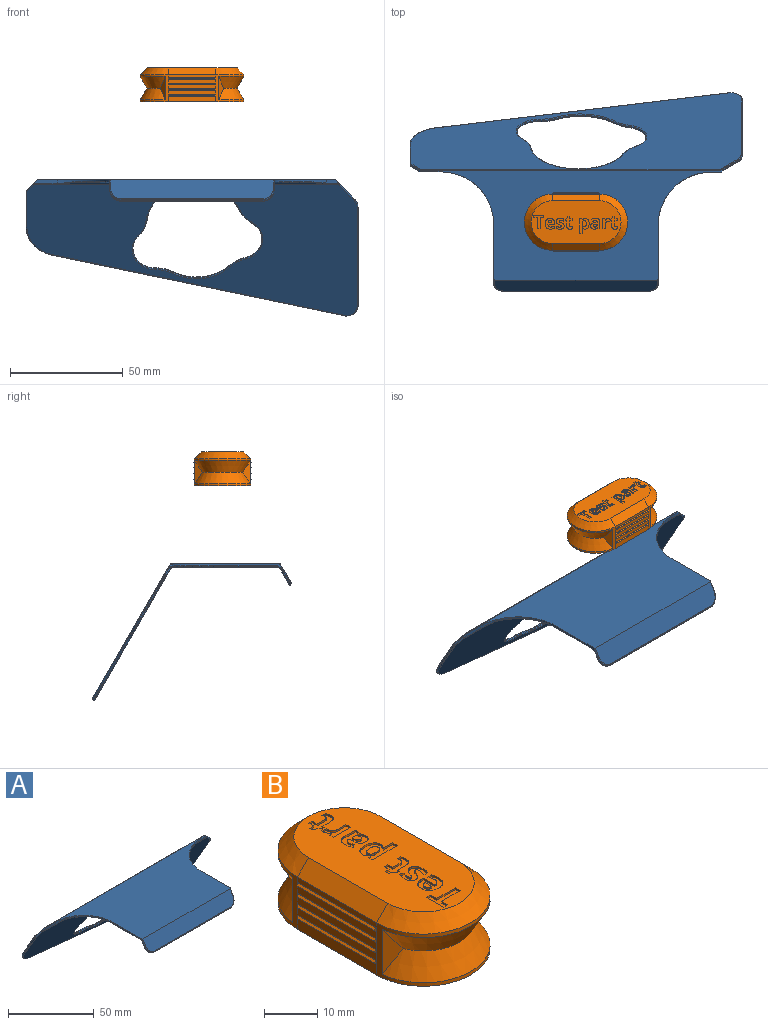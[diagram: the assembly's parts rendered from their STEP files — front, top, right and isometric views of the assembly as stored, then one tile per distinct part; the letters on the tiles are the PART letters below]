
ASSEMBLY  parts=2 mates=1
PART A: 114 faces, bbox 149.3x90x61.8 mm
  f0: plane 45.29x19.46mm, normal (0,0,-1), area 244.4mm2, adj f74,f79,f80,f83,f84
  f1: plane 45.5x44.32mm, normal (0,0,-1), area 2016.7mm2, adj f35,f36,f38,f39
  f2: plane 146.7x58.15mm, normal (0,-0.87,-0.5), area 5367.5mm2, adj f54,f55,f56,f57,f58,f61,f62,f63
  f3: plane 44.06x25.78mm, normal (1,0,0), area 20.3mm2, adj f27,f28,f76,f98
  f4: plane 146.7x59.51mm, normal (0,0.87,0.5), area 5569.3mm2, adj f97,f98,f99,f100,f101,f102,f103,f104
  f5: plane 63x0.4mm, normal (0,-0.87,-0.5), area 29.1mm2, adj f29,f30,f53,f94
  f6: plane 72.2x7.19mm, normal (0,0.87,-0.5), area 589.3mm2, adj f35,f49,f51,f53,f60,f65
  f7: plane 45.29x18.08mm, normal (0,0,-1), area 201.8mm2, adj f41,f42,f43,f45,f46
  f8: plane 132.6x48.75mm, normal (0,0,1), area 3825.2mm2, adj f9,f19,f20,f21,f22,f23,f24,f26
  f9: plane 72.2x8.46mm, normal (0,-0.87,0.5), area 694.8mm2, adj f8,f92,f93,f94,f95,f96
  f10: plane 15.74x9.42mm, normal (-1,0,0), area 7.2mm2, adj f33,f34,f55,f58,f103
  f11: cylinder r=15mm len=7.28mm, axis (0,0.87,0.5), area 3.6mm2, adj f12,f18,f63,f109
  f12: cylinder r=21.25mm len=40.75mm, axis (0,0.87,0.5), area 23.3mm2, adj f11,f13,f68,f73,f77,f78,f82,f107
  f13: cylinder r=15mm len=6.18mm, axis (0,0.87,0.5), area 3.6mm2, adj f12,f14,f72,f106
  f14: cylinder r=10mm len=15.86mm, axis (0,0.87,0.5), area 9.3mm2, adj f13,f15,f67,f108
  f15: cylinder r=15mm len=6.87mm, axis (0,0.87,0.5), area 3.2mm2, adj f14,f16,f62,f110
  f16: cylinder r=20.94mm len=25.13mm, axis (0,0.87,0.5), area 10.9mm2, adj f15,f17,f56,f112
  f17: cylinder r=15mm len=7.65mm, axis (0,0.87,0.5), area 3.2mm2, adj f16,f18,f54,f113
  f18: cylinder r=10mm len=14.64mm, axis (0,0.87,0.5), area 9.3mm2, adj f11,f17,f57,f111
  f19: cylinder r=23.5mm len=23.5mm, axis (0,0,-1), area 32.3mm2, adj f8,f20,f21,f45,f48,f50
  f20: plane 26.5x4.46mm, normal (-1,0,0), area 21.7mm2, adj f8,f19,f29,f42,f44,f47,f49,f92
  f21: plane 10.07x1.59mm, normal (0,-1,0), area 14.4mm2, adj f8,f19,f34,f52,f59
  f22: cylinder r=23.5mm len=23.5mm, axis (0,0,-1), area 31.6mm2, adj f8,f23,f24,f84,f87,f89
  f23: plane 26.33x4.46mm, normal (1,0,0), area 21.5mm2, adj f8,f22,f30,f65,f70,f75,f80,f96
  f24: plane 5.16x1.5mm, normal (0.01,-1,0), area 6.6mm2, adj f8,f22,f26,f90,f91
  f25: plane 129.83x27.19mm, normal (-0.23,0.49,-0.84), area 53.4mm2, adj f28,f33,f66,f99
  f26: plane 8.54x8.54mm, normal (0.71,0,0.71), area 6.4mm2, adj f8,f24,f27,f85,f88,f90,f102
  f27: cylinder r=5mm len=3.54mm, axis (0,-1,0), area 1.8mm2, adj f3,f26,f81,f100
  f28: cylinder r=5mm len=6.17mm, axis (0,0.87,0.5), area 3.6mm2, adj f3,f25,f71,f97
  f29: cylinder r=5mm len=5.89mm, axis (0,0.5,-0.87), area 3.6mm2, adj f5,f20,f51,f93
  f30: cylinder r=5mm len=5.89mm, axis (0,-0.5,0.87), area 3.6mm2, adj f5,f23,f60,f95
  f31: plane 47.23x10mm, normal (0,0,-1), area 472.3mm2, adj f35,f36,f37,f38
  f32: plane 47.23x10mm, normal (0,0,-1), area 472.3mm2, adj f35,f36,f39,f40
  f33: cylinder r=15mm len=12.83mm, axis (0,-0.87,-0.5), area 8mm2, adj f10,f25,f61,f101
  f34: plane 5.17x5.17mm, normal (-0.71,0,0.71), area 3.8mm2, adj f8,f10,f21,f58,f59,f64,f103,f105
  f35: plane 72.21x1.51mm, normal (0,0.5,-0.87), area 103.4mm2, adj f1,f6,f31,f32,f37,f38,f39,f40
  f36: plane 134.71x1.42mm, normal (0,-0.5,-0.87), area 162.1mm2, adj f1,f31,f32,f37,f38,f39,f40,f43
  f37: plane 47.23x0.38mm, normal (-0.71,0,-0.71), area 25.2mm2, adj f31,f35,f36,f43
  f38: plane 47.23x0.5mm, normal (0.71,0,-0.71), area 32.8mm2, adj f1,f31,f35,f36
  f39: plane 47.23x0.5mm, normal (-0.71,0,-0.71), area 32.8mm2, adj f1,f32,f35,f36
  f40: plane 47.23x0.38mm, normal (0.71,0,-0.71), area 25.2mm2, adj f32,f35,f36,f79
  f41: cylinder r=0.4mm len=2.53mm, axis (1,0,0), area 0.5mm2, adj f7,f35,f43,f44
  f42: cylinder r=0.4mm len=22.82mm, axis (0,1,0), area 14.3mm2, adj f7,f20,f44,f45
  f43: cylinder r=0.4mm len=45.91mm, axis (0,-1,0), area 14.3mm2, adj f7,f35,f36,f37,f41,f46
  f44: torus R=0.8mm, axis (1,0,0), area 0.2mm2, adj f20,f41,f42,f47
  f45: torus R=23.9mm, axis (0,0,-1), area 18.2mm2, adj f7,f19,f42,f48
  f46: cylinder r=0.4mm len=19.48mm, axis (1,0,0), area 3.9mm2, adj f7,f36,f43,f48
  f47: cylinder r=0.4mm len=1.7mm, axis (0,0.87,0.5), area 1.1mm2, adj f20,f35,f44,f49
  f48: bspline ~2.03x0.75mm, area 0.6mm2, adj f19,f45,f46,f50
  f49: cylinder r=0.4mm len=2.89mm, axis (0,0.5,0.87), area 1.9mm2, adj f6,f20,f47,f51
  f50: bspline ~6.89x1.22mm, area 2.9mm2, adj f19,f36,f48,f52
  f51: bspline ~5.61x5.01mm, area 6.2mm2, adj f6,f29,f49,f53
  f52: cylinder r=0.4mm len=9.99mm, axis (1,0,0), area 4.1mm2, adj f21,f36,f50,f59
  f53: cylinder r=0.4mm len=63mm, axis (-1,0,0), area 52.8mm2, adj f5,f6,f51,f60
  f54: torus R=14.6mm, axis (0,0.87,0.5), area 5mm2, adj f2,f17,f56,f57
  f55: cylinder r=0.4mm len=15.89mm, axis (0,0.5,-0.87), area 11.3mm2, adj f2,f10,f58,f61
  f56: torus R=21.34mm, axis (0,0.87,0.5), area 17.2mm2, adj f2,f16,f54,f62
  f57: torus R=10.4mm, axis (0,0.87,0.5), area 14.8mm2, adj f2,f18,f54,f63
  f58: cylinder r=0.4mm len=3.81mm, axis (-0.65,0.38,-0.65), area 3.9mm2, adj f2,f10,f34,f55,f64
  f59: cylinder r=0.4mm len=1mm, axis (0.45,-0.77,0.45), area 0.5mm2, adj f21,f34,f36,f52,f64
  f60: bspline ~5.61x5.24mm, area 6.2mm2, adj f6,f30,f53,f65
  f61: torus R=14.6mm, axis (0,0.87,0.5), area 12.5mm2, adj f2,f33,f55,f66
  f62: torus R=14.6mm, axis (0,0.87,0.5), area 5mm2, adj f2,f15,f56,f67
  f63: torus R=14.6mm, axis (0,0.87,0.5), area 5.7mm2, adj f2,f11,f57,f68
  f64: bspline ~0.91x0.87mm, area 0.4mm2, adj f34,f58,f59,f69
  f65: cylinder r=0.4mm len=2.89mm, axis (0,-0.5,-0.87), area 1.9mm2, adj f6,f23,f60,f70
  f66: cylinder r=0.4mm len=129.93mm, axis (-0.97,-0.12,0.2), area 83.9mm2, adj f2,f25,f61,f71
  f67: torus R=10.4mm, axis (0,0.87,0.5), area 14.8mm2, adj f2,f14,f62,f72
  f68: torus R=21.65mm, axis (0,0.87,0.5), area 16mm2, adj f2,f12,f63,f73
  f69: cylinder r=0.4mm len=67.67mm, axis (1,0,0), area 13.9mm2, adj f2,f36,f64,f73
  f70: cylinder r=0.4mm len=1.7mm, axis (0,-0.87,-0.5), area 1.1mm2, adj f23,f35,f65,f75
  f71: torus R=4.6mm, axis (0,0.87,0.5), area 5.5mm2, adj f2,f28,f66,f76
  f72: torus R=14.6mm, axis (0,0.87,0.5), area 5.7mm2, adj f2,f13,f67,f77
  f73: bspline ~3.47x0.83mm, area 1mm2, adj f12,f68,f69,f78
  f74: cylinder r=0.4mm len=3.41mm, axis (1,0,0), area 0.7mm2, adj f0,f35,f75,f79
  f75: torus R=0.8mm, axis (-1,0,0), area 0.2mm2, adj f23,f70,f74,f80
  f76: cylinder r=0.4mm len=44.26mm, axis (0,-0.5,0.87), area 32mm2, adj f2,f3,f71,f81
  f77: torus R=21.65mm, axis (0,0.87,0.5), area 12.5mm2, adj f2,f12,f72,f82
  f78: bspline ~7.18x0.7mm, area 3mm2, adj f12,f36,f73,f82
  f79: cylinder r=0.4mm len=45.91mm, axis (0,-1,0), area 14.3mm2, adj f0,f35,f36,f40,f74,f83
  f80: cylinder r=0.4mm len=22.64mm, axis (0,-1,0), area 14.2mm2, adj f0,f23,f75,f84
  f81: bspline ~3.74x2.25mm, area 3mm2, adj f2,f27,f76,f85
  f82: bspline ~3.48x0.83mm, area 1mm2, adj f12,f77,f78,f86
  f83: cylinder r=0.4mm len=20.97mm, axis (1,0,0), area 4.2mm2, adj f0,f36,f79,f87
  f84: torus R=23.9mm, axis (0,0,-1), area 18.5mm2, adj f0,f22,f80,f87
  f85: cylinder r=0.4mm len=7.34mm, axis (0.65,0.38,-0.65), area 8.1mm2, adj f2,f26,f81,f88
  f86: cylinder r=0.4mm len=60.44mm, axis (1,0,0), area 12.4mm2, adj f2,f36,f82,f88
  f87: bspline ~1.94x0.71mm, area 0.7mm2, adj f22,f83,f84,f89
  f88: bspline ~0.95x0.92mm, area 0.3mm2, adj f26,f85,f86,f90
  f89: bspline ~6.09x1.04mm, area 2.6mm2, adj f22,f36,f87,f91
  f90: cylinder r=0.4mm len=1.1mm, axis (-0.45,-0.77,0.45), area 0.7mm2, adj f24,f26,f36,f88,f91
  f91: cylinder r=0.4mm len=5.08mm, axis (-1,-0.01,0.01), area 2.1mm2, adj f24,f36,f89,f90
  f92: cylinder r=0.4mm len=4.26mm, axis (0,-0.5,-0.87), area 2.9mm2, adj f8,f9,f20,f93
  f93: bspline ~5x5mm, area 4.1mm2, adj f9,f29,f92,f94
  f94: cylinder r=0.4mm len=63mm, axis (1,0,0), area 26.4mm2, adj f5,f9,f93,f95
  f95: bspline ~5x5mm, area 4.1mm2, adj f9,f30,f94,f96
  f96: cylinder r=0.4mm len=4.26mm, axis (0,0.5,0.87), area 2.9mm2, adj f8,f9,f23,f95
  f97: torus R=4.6mm, axis (0,0.87,0.5), area 5.5mm2, adj f4,f28,f98,f99
  f98: cylinder r=0.4mm len=44.06mm, axis (0,0.5,-0.87), area 31.8mm2, adj f3,f4,f97,f100
  f99: cylinder r=0.4mm len=129.93mm, axis (-0.97,-0.12,0.2), area 83.9mm2, adj f4,f25,f97,f101
  f100: bspline ~5.02x3.02mm, area 2.3mm2, adj f4,f27,f98,f102
  f101: torus R=14.6mm, axis (0,0.87,0.5), area 12.5mm2, adj f4,f33,f99,f103
  f102: cylinder r=0.4mm len=8.82mm, axis (0.65,0.38,-0.65), area 6.3mm2, adj f4,f8,f26,f100,f104
  f103: cylinder r=0.4mm len=15.72mm, axis (0,-0.5,0.87), area 11.2mm2, adj f4,f10,f34,f101,f105
  f104: cylinder r=0.4mm len=132.49mm, axis (1,0,0), area 55.4mm2, adj f4,f8,f102,f105
  f105: cylinder r=0.4mm len=5.26mm, axis (-0.65,0.38,-0.65), area 3.6mm2, adj f4,f8,f34,f103,f104
  f106: torus R=14.6mm, axis (0,0.87,0.5), area 5.7mm2, adj f4,f13,f107,f108
  f107: torus R=21.65mm, axis (0,0.87,0.5), area 35.4mm2, adj f4,f12,f106,f109
  f108: torus R=10.4mm, axis (0,0.87,0.5), area 14.8mm2, adj f4,f14,f106,f110
  f109: torus R=14.6mm, axis (0,0.87,0.5), area 5.7mm2, adj f4,f11,f107,f111
  f110: torus R=14.6mm, axis (0,0.87,0.5), area 5mm2, adj f4,f15,f108,f112
  f111: torus R=10.4mm, axis (0,0.87,0.5), area 14.8mm2, adj f4,f18,f109,f113
  f112: torus R=21.34mm, axis (0,0.87,0.5), area 17.2mm2, adj f4,f16,f110,f113
  f113: torus R=14.6mm, axis (0,0.87,0.5), area 5mm2, adj f4,f17,f111,f112
PART B: 256 faces, bbox 26x46x15 mm
  f0: plane 40x19mm, normal (0,0,1), area 585.2mm2, adj f17,f18,f19,f20,f93,f94,f95,f96
  f1: plane 21x2.5mm, normal (1,0,0), area 52.5mm2, adj f10,f12,f14,f60
  f2: plane 21x1.7mm, normal (1,0,0), area 35.7mm2, adj f10,f12,f56,f58
  f3: plane 21x1.7mm, normal (1,0,0), area 35.7mm2, adj f10,f12,f52,f54
  f4: plane 21x1.7mm, normal (1,0,0), area 35.7mm2, adj f10,f12,f48,f50
  f5: plane 21x2.5mm, normal (-1,0,0), area 52.5mm2, adj f10,f12,f14,f42
  f6: plane 21x1.7mm, normal (-1,0,0), area 35.7mm2, adj f10,f12,f38,f44
  f7: plane 21x1.7mm, normal (-1,0,0), area 35.7mm2, adj f10,f12,f34,f40
  f8: plane 21x1.7mm, normal (-1,0,0), area 35.7mm2, adj f10,f12,f30,f36
  f9: cylinder r=10.5mm len=21mm, axis (0,0,-1), area 679.5mm2, adj f15,f255
  f10: cylinder r=12.5mm len=25mm, axis (0,0,-1), area 92.6mm2, adj f1,f2,f3,f4,f5,f6,f7,f8
  f11: plane 21x1.2mm, normal (-1,0,0), area 25.2mm2, adj f10,f12,f17,f32
  f12: cylinder r=12.5mm len=25mm, axis (0,0,-1), area 92.6mm2, adj f1,f2,f3,f4,f5,f6,f7,f8
  f13: plane 21x1.2mm, normal (1,0,0), area 25.2mm2, adj f10,f12,f20,f46
  f14: plane 46x25mm, normal (0,0,-1), area 600.4mm2, adj f1,f5,f10,f12,f15
  f15: cone r=11.5mm half-angle=45deg, axis (0,0,-1), area 97.7mm2, adj f9,f14
  f16: plane 6x6mm, normal (0,0,-1), area 28.3mm2, adj f255
  f17: plane 21x3mm, normal (-0.71,0,0.71), area 89.1mm2, adj f0,f11,f18,f19
  f18: cone r=9.5mm half-angle=45deg, axis (0,0,-1), area 146.6mm2, adj f0,f10,f17,f20
  f19: cone r=9.5mm half-angle=45deg, axis (0,0,-1), area 146.6mm2, adj f0,f12,f17,f20
  f20: plane 21x3mm, normal (0.71,0,0.71), area 89.1mm2, adj f0,f13,f18,f19
  f21: cone r=9.5mm half-angle=30deg, axis (0,0,1), area 177.8mm2, adj f10,f22,f27,f28
  f22: cone r=13.83mm half-angle=30deg, axis (0,0,-1), area 177.8mm2, adj f10,f21,f27,f28
  f23: cone r=9.5mm half-angle=30deg, axis (0,0,1), area 177.8mm2, adj f12,f24,f25,f26
  f24: cone r=13.83mm half-angle=30deg, axis (0,0,-1), area 177.8mm2, adj f12,f23,f25,f26
  f25: plane 10.39x3.6mm, normal (-0.51,-0.86,0), area 20.8mm2, adj f12,f23,f24
  f26: plane 10.39x3.6mm, normal (0.51,-0.86,0), area 20.8mm2, adj f12,f23,f24
  f27: plane 10.39x3.6mm, normal (0.51,0.86,0), area 20.8mm2, adj f10,f21,f22
  f28: plane 10.39x3.6mm, normal (-0.51,0.86,0), area 20.8mm2, adj f10,f21,f22
  f29: plane 0.8x0.1mm, normal (0,1,0), area 0.1mm2, adj f10,f30,f32,f77
  f30: plane 21x0.1mm, normal (0,0,-1), area 2.1mm2, adj f8,f29,f31,f79
  f31: plane 0.8x0.1mm, normal (0,-1,0), area 0.1mm2, adj f12,f30,f32,f80
  f32: plane 21x0.1mm, normal (0,0,1), area 2.1mm2, adj f11,f29,f31,f78
  f33: plane 0.8x0.1mm, normal (0,1,0), area 0.1mm2, adj f10,f34,f36,f84
  f34: plane 21x0.1mm, normal (0,0,-1), area 2.1mm2, adj f7,f33,f35,f83
  f35: plane 0.8x0.1mm, normal (0,-1,0), area 0.1mm2, adj f12,f34,f36,f81
  f36: plane 21x0.1mm, normal (0,0,1), area 2.1mm2, adj f8,f33,f35,f82
  f37: plane 0.8x0.1mm, normal (0,1,0), area 0.1mm2, adj f10,f38,f40,f92
  f38: plane 21x0.1mm, normal (0,0,-1), area 2.1mm2, adj f6,f37,f39,f91
  f39: plane 0.8x0.1mm, normal (0,-1,0), area 0.1mm2, adj f12,f38,f40,f89
  f40: plane 21x0.1mm, normal (0,0,1), area 2.1mm2, adj f7,f37,f39,f90
  f41: plane 0.8x0.1mm, normal (0,1,0), area 0.1mm2, adj f10,f42,f44,f88
  f42: plane 21x0.1mm, normal (0,0,-1), area 2.1mm2, adj f5,f41,f43,f87
  f43: plane 0.8x0.1mm, normal (0,-1,0), area 0.1mm2, adj f12,f42,f44,f85
  f44: plane 21x0.1mm, normal (0,0,1), area 2.1mm2, adj f6,f41,f43,f86
  f45: plane 0.8x0.1mm, normal (0,1,0), area 0.1mm2, adj f10,f46,f48,f73
  f46: plane 21x0.1mm, normal (0,0,1), area 2.1mm2, adj f13,f45,f47,f74
  f47: plane 0.8x0.1mm, normal (0,-1,0), area 0.1mm2, adj f12,f46,f48,f76
  f48: plane 21x0.1mm, normal (0,0,-1), area 2.1mm2, adj f4,f45,f47,f75
  f49: plane 0.8x0.1mm, normal (0,1,0), area 0.1mm2, adj f10,f50,f52,f72
  f50: plane 21x0.1mm, normal (0,0,1), area 2.1mm2, adj f4,f49,f51,f70
  f51: plane 0.8x0.1mm, normal (0,-1,0), area 0.1mm2, adj f12,f50,f52,f69
  f52: plane 21x0.1mm, normal (0,0,-1), area 2.1mm2, adj f3,f49,f51,f71
  f53: plane 0.8x0.1mm, normal (0,1,0), area 0.1mm2, adj f10,f54,f56,f68
  f54: plane 21x0.1mm, normal (0,0,1), area 2.1mm2, adj f3,f53,f55,f66
  f55: plane 0.8x0.1mm, normal (0,-1,0), area 0.1mm2, adj f12,f54,f56,f65
  f56: plane 21x0.1mm, normal (0,0,-1), area 2.1mm2, adj f2,f53,f55,f67
  f57: plane 0.8x0.1mm, normal (0,1,0), area 0.1mm2, adj f10,f58,f60,f64
  f58: plane 21x0.1mm, normal (0,0,1), area 2.1mm2, adj f2,f57,f59,f62
  f59: plane 0.8x0.1mm, normal (0,-1,0), area 0.1mm2, adj f12,f58,f60,f61
  f60: plane 21x0.1mm, normal (0,0,-1), area 2.1mm2, adj f1,f57,f59,f63
  f61: plane 0.8x0.4mm, normal (0.71,-0.71,0), area 0.2mm2, adj f59,f62,f63
  f62: plane 21x0.4mm, normal (0.71,0,0.71), area 11.7mm2, adj f58,f61,f63,f64
  f63: plane 21x0.4mm, normal (0.71,0,-0.71), area 11.7mm2, adj f60,f61,f62,f64
  f64: plane 0.8x0.4mm, normal (0.71,0.71,0), area 0.2mm2, adj f57,f62,f63
  f65: plane 0.8x0.4mm, normal (0.71,-0.71,0), area 0.2mm2, adj f55,f66,f67
  f66: plane 21x0.4mm, normal (0.71,0,0.71), area 11.7mm2, adj f54,f65,f67,f68
  f67: plane 21x0.4mm, normal (0.71,0,-0.71), area 11.7mm2, adj f56,f65,f66,f68
  f68: plane 0.8x0.4mm, normal (0.71,0.71,0), area 0.2mm2, adj f53,f66,f67
  f69: plane 0.8x0.4mm, normal (0.71,-0.71,0), area 0.2mm2, adj f51,f70,f71
  f70: plane 21x0.4mm, normal (0.71,0,0.71), area 11.7mm2, adj f50,f69,f71,f72
  f71: plane 21x0.4mm, normal (0.71,0,-0.71), area 11.7mm2, adj f52,f69,f70,f72
  f72: plane 0.8x0.4mm, normal (0.71,0.71,0), area 0.2mm2, adj f49,f70,f71
  f73: plane 0.8x0.4mm, normal (0.71,0.71,0), area 0.2mm2, adj f45,f74,f75
  f74: plane 21x0.4mm, normal (0.71,0,0.71), area 11.7mm2, adj f46,f73,f75,f76
  f75: plane 21x0.4mm, normal (0.71,0,-0.71), area 11.7mm2, adj f48,f73,f74,f76
  f76: plane 0.8x0.4mm, normal (0.71,-0.71,0), area 0.2mm2, adj f47,f74,f75
  f77: plane 0.8x0.4mm, normal (-0.71,0.71,0), area 0.2mm2, adj f29,f78,f79
  f78: plane 21x0.4mm, normal (-0.71,0,0.71), area 11.7mm2, adj f32,f77,f79,f80
  f79: plane 21x0.4mm, normal (-0.71,0,-0.71), area 11.7mm2, adj f30,f77,f78,f80
  f80: plane 0.8x0.4mm, normal (-0.71,-0.71,0), area 0.2mm2, adj f31,f78,f79
  f81: plane 0.8x0.4mm, normal (-0.71,-0.71,0), area 0.2mm2, adj f35,f82,f83
  f82: plane 21x0.4mm, normal (-0.71,0,0.71), area 11.7mm2, adj f36,f81,f83,f84
  f83: plane 21x0.4mm, normal (-0.71,0,-0.71), area 11.7mm2, adj f34,f81,f82,f84
  f84: plane 0.8x0.4mm, normal (-0.71,0.71,0), area 0.2mm2, adj f33,f82,f83
  f85: plane 0.8x0.4mm, normal (-0.71,-0.71,0), area 0.2mm2, adj f43,f86,f87
  f86: plane 21x0.4mm, normal (-0.71,0,0.71), area 11.7mm2, adj f44,f85,f87,f88
  f87: plane 21x0.4mm, normal (-0.71,0,-0.71), area 11.7mm2, adj f42,f85,f86,f88
  f88: plane 0.8x0.4mm, normal (-0.71,0.71,0), area 0.2mm2, adj f41,f86,f87
  f89: plane 0.8x0.4mm, normal (-0.71,-0.71,0), area 0.2mm2, adj f39,f90,f91
  f90: plane 21x0.4mm, normal (-0.71,0,0.71), area 11.7mm2, adj f40,f89,f91,f92
  f91: plane 21x0.4mm, normal (-0.71,0,-0.71), area 11.7mm2, adj f38,f89,f90,f92
  f92: plane 0.8x0.4mm, normal (-0.71,0.71,0), area 0.2mm2, adj f37,f90,f91
  f93: extruded ~1.08x0.49mm, area 0.5mm2, adj f0,f94,f118,f119
  f94: extruded ~0.59x0.4mm, area 0.2mm2, adj f0,f93,f95,f119
  f95: extruded ~0.44x0.4mm, area 0.2mm2, adj f0,f94,f96,f119
  f96: extruded ~0.79x0.41mm, area 0.4mm2, adj f0,f95,f97,f119
  f97: extruded ~0.78x0.4mm, area 0.3mm2, adj f0,f96,f98,f119
  f98: extruded ~0.4x0.29mm, area 0.1mm2, adj f0,f97,f99,f119
  f99: extruded ~0.55x0.4mm, area 0.3mm2, adj f0,f98,f100,f119
  f100: extruded ~0.61x0.4mm, area 0.2mm2, adj f0,f99,f101,f119
  f101: extruded ~0.65x0.4mm, area 0.3mm2, adj f0,f100,f102,f119
  f102: plane 0.9x0.4mm, normal (-0.39,-0.92,0), area 0.4mm2, adj f0,f101,f103,f119
  f103: extruded ~1.61x0.4mm, area 0.7mm2, adj f0,f102,f104,f119
  f104: extruded ~1.35x0.4mm, area 0.6mm2, adj f0,f103,f105,f119
  f105: extruded ~0.95x0.47mm, area 0.4mm2, adj f0,f104,f106,f119
  f106: extruded ~0.6x0.4mm, area 0.2mm2, adj f0,f105,f107,f119
  f107: extruded ~0.43x0.4mm, area 0.2mm2, adj f0,f106,f108,f119
  f108: extruded ~0.78x0.41mm, area 0.4mm2, adj f0,f107,f109,f119
  f109: extruded ~0.59x0.4mm, area 0.3mm2, adj f0,f108,f110,f119
  f110: extruded ~0.4x0.31mm, area 0.2mm2, adj f0,f109,f111,f119
  f111: extruded ~0.4x0.24mm, area 0.1mm2, adj f0,f110,f112,f119
  f112: extruded ~0.68x0.4mm, area 0.4mm2, adj f0,f111,f113,f119
  f113: extruded ~0.77x0.4mm, area 0.3mm2, adj f0,f112,f114,f119
  f114: extruded ~0.79x0.4mm, area 0.3mm2, adj f0,f113,f115,f119
  f115: plane 1.03x0.4mm, normal (0,1,0), area 0.4mm2, adj f0,f114,f116,f119
  f116: extruded ~0.66x0.4mm, area 0.3mm2, adj f0,f115,f117,f119
  f117: extruded ~0.85x0.4mm, area 0.3mm2, adj f0,f116,f118,f119
  f118: extruded ~1.47x0.4mm, area 0.6mm2, adj f0,f93,f117,f119
  f119: plane 4.76x3.48mm, normal (0,0,1), area 10.6mm2, adj f93,f94,f95,f96,f97,f98,f99,f100
  f120: extruded ~0.79x0.4mm, area 0.3mm2, adj f0,f121,f137,f138
  f121: extruded ~0.4x0.4mm, area 0.2mm2, adj f0,f120,f122,f138
  f122: extruded ~0.4x0.39mm, area 0.2mm2, adj f0,f121,f123,f138
  f123: plane 2.21x0.4mm, normal (0,-1,0), area 0.9mm2, adj f0,f122,f124,f138
  f124: plane 1.29x0.4mm, normal (-1,0,0), area 0.5mm2, adj f0,f123,f125,f138
  f125: plane 0.94x0.4mm, normal (0,-1,0), area 0.4mm2, adj f0,f124,f126,f138
  f126: plane 1.29x0.4mm, normal (1,0,0), area 0.5mm2, adj f0,f125,f127,f138
  f127: plane 0.98x0.4mm, normal (0,-1,0), area 0.4mm2, adj f0,f126,f128,f138
  f128: plane 0.8x0.4mm, normal (1,0,0), area 0.3mm2, adj f0,f127,f129,f138
  f129: plane 0.97x0.4mm, normal (0.35,0.94,0), area 0.4mm2, adj f0,f128,f130,f138
  f130: plane 0.69x0.42mm, normal (0.85,0.52,0), area 0.3mm2, adj f0,f129,f131,f138
  f131: plane 0.53x0.4mm, normal (0,1,0), area 0.2mm2, adj f0,f130,f132,f138
  f132: plane 0.6x0.4mm, normal (-1,0,0), area 0.2mm2, adj f0,f131,f133,f138
  f133: plane 2.21x0.4mm, normal (0,1,0), area 0.9mm2, adj f0,f132,f134,f138
  f134: extruded ~1.14x0.4mm, area 0.5mm2, adj f0,f133,f135,f138
  f135: extruded ~1.09x0.4mm, area 0.5mm2, adj f0,f134,f136,f138
  f136: extruded ~1.15x0.4mm, area 0.5mm2, adj f0,f135,f137,f138
  f137: plane 0.93x0.4mm, normal (0,-1,0), area 0.4mm2, adj f0,f120,f136,f138
  f138: plane 5.65x3.19mm, normal (0,0,1), area 9.4mm2, adj f120,f121,f122,f123,f124,f125,f126,f127
  f139: extruded ~0.42x0.4mm, area 0.2mm2, adj f0,f140,f151,f152
  f140: extruded ~0.79x0.4mm, area 0.3mm2, adj f0,f139,f141,f152
  f141: extruded ~0.62x0.58mm, area 0.3mm2, adj f0,f140,f142,f152
  f142: plane 0.4x0.06mm, normal (1,0,0), area 0mm2, adj f0,f141,f143,f152
  f143: plane 0.77x0.4mm, normal (0.23,-0.97,0), area 0.3mm2, adj f0,f142,f144,f152
  f144: plane 0.95x0.4mm, normal (1,0,0), area 0.4mm2, adj f0,f143,f145,f152
  f145: plane 4.59x0.4mm, normal (0,1,0), area 1.8mm2, adj f0,f144,f146,f152
  f146: plane 1.25x0.4mm, normal (-1,0,0), area 0.5mm2, adj f0,f145,f147,f152
  f147: plane 2.34x0.4mm, normal (0,-1,0), area 0.9mm2, adj f0,f146,f148,f152
  f148: extruded ~0.86x0.4mm, area 0.4mm2, adj f0,f147,f149,f152
  f149: extruded ~0.93x0.4mm, area 0.4mm2, adj f0,f148,f150,f152
  f150: extruded ~0.4x0.37mm, area 0.1mm2, adj f0,f149,f151,f152
  f151: plane 1.17x0.4mm, normal (-0.08,-1,0), area 0.5mm2, adj f0,f139,f150,f152
  f152: plane 4.68x2.99mm, normal (0,0,1), area 7.5mm2, adj f139,f140,f141,f142,f143,f144,f145,f146
  f153: extruded ~0.79x0.4mm, area 0.3mm2, adj f0,f154,f170,f171
  f154: extruded ~0.4x0.4mm, area 0.2mm2, adj f0,f153,f155,f171
  f155: extruded ~0.4x0.39mm, area 0.2mm2, adj f0,f154,f156,f171
  f156: plane 2.21x0.4mm, normal (0,-1,0), area 0.9mm2, adj f0,f155,f157,f171
  f157: plane 1.29x0.4mm, normal (-1,0,0), area 0.5mm2, adj f0,f156,f158,f171
  f158: plane 0.94x0.4mm, normal (0,-1,0), area 0.4mm2, adj f0,f157,f159,f171
  f159: plane 1.29x0.4mm, normal (1,0,0), area 0.5mm2, adj f0,f158,f160,f171
  f160: plane 0.98x0.4mm, normal (0,-1,0), area 0.4mm2, adj f0,f159,f161,f171
  f161: plane 0.8x0.4mm, normal (1,0,0), area 0.3mm2, adj f0,f160,f162,f171
  f162: plane 0.97x0.4mm, normal (0.35,0.94,0), area 0.4mm2, adj f0,f161,f163,f171
  f163: plane 0.69x0.42mm, normal (0.85,0.52,0), area 0.3mm2, adj f0,f162,f164,f171
  f164: plane 0.53x0.4mm, normal (0,1,0), area 0.2mm2, adj f0,f163,f165,f171
  f165: plane 0.6x0.4mm, normal (-1,0,0), area 0.2mm2, adj f0,f164,f166,f171
  f166: plane 2.21x0.4mm, normal (0,1,0), area 0.9mm2, adj f0,f165,f167,f171
  f167: extruded ~1.14x0.4mm, area 0.5mm2, adj f0,f166,f168,f171
  f168: extruded ~1.09x0.4mm, area 0.5mm2, adj f0,f167,f169,f171
  f169: extruded ~1.15x0.4mm, area 0.5mm2, adj f0,f168,f170,f171
  f170: plane 0.93x0.4mm, normal (0,-1,0), area 0.4mm2, adj f0,f153,f169,f171
  f171: plane 5.65x3.19mm, normal (0,0,1), area 9.4mm2, adj f153,f154,f155,f156,f157,f158,f159,f160
  f172: extruded ~1.73x0.61mm, area 0.8mm2, adj f0,f173,f191,f192
  f173: extruded ~0.91x0.4mm, area 0.4mm2, adj f0,f172,f174,f192
  f174: extruded ~0.7x0.4mm, area 0.3mm2, adj f0,f173,f175,f192
  f175: plane 0.97x0.4mm, normal (0,-1,0), area 0.4mm2, adj f0,f174,f176,f192
  f176: extruded ~0.77x0.4mm, area 0.3mm2, adj f0,f175,f177,f192
  f177: extruded ~0.78x0.4mm, area 0.3mm2, adj f0,f176,f178,f192
  f178: extruded ~0.83x0.4mm, area 0.4mm2, adj f0,f177,f179,f192
  f179: extruded ~0.83x0.4mm, area 0.4mm2, adj f0,f178,f180,f192
  f180: plane 2.96x0.4mm, normal (-1,0,0), area 1.2mm2, adj f0,f179,f181,f192
  f181: plane 0.61x0.4mm, normal (0,-1,0), area 0.2mm2, adj f0,f180,f182,f192
  f182: extruded ~1.53x0.54mm, area 0.7mm2, adj f0,f181,f183,f192
  f183: extruded ~1.51x0.55mm, area 0.7mm2, adj f0,f182,f184,f192
  f184: extruded ~1.6x0.63mm, area 0.7mm2, adj f0,f183,f185,f192
  f185: extruded ~1.78x0.58mm, area 0.8mm2, adj f0,f184,f191,f192
  f186: extruded ~0.62x0.4mm, area 0.3mm2, adj f187,f190,f192,f193
  f187: extruded ~0.63x0.4mm, area 0.3mm2, adj f186,f188,f192,f193
  f188: extruded ~0.72x0.4mm, area 0.3mm2, adj f187,f189,f192,f193
  f189: plane 1.76x0.4mm, normal (1,0,0), area 0.7mm2, adj f188,f190,f192,f193
  f190: extruded ~0.72x0.4mm, area 0.3mm2, adj f186,f189,f192,f193
  f191: extruded ~1.73x0.62mm, area 0.8mm2, adj f0,f172,f185,f192
  f192: plane 4.76x4.23mm, normal (0,0,1), area 12.7mm2, adj f172,f173,f174,f175,f176,f177,f178,f179
  f193: plane 1.76x0.97mm, normal (0,0,1), area 1.4mm2, adj f186,f187,f188,f189,f190
  f194: extruded ~0.68x0.4mm, area 0.3mm2, adj f195,f216,f217,f253
  f195: extruded ~0.65x0.4mm, area 0.3mm2, adj f194,f196,f217,f253
  f196: extruded ~1.02x0.4mm, area 0.4mm2, adj f195,f197,f217,f253
  f197: extruded ~1.39x0.84mm, area 0.7mm2, adj f196,f198,f217,f253
  f198: extruded ~0.7x0.4mm, area 0.3mm2, adj f197,f199,f217,f253
  f199: extruded ~1.06x0.4mm, area 0.4mm2, adj f198,f200,f217,f253
  f200: plane 0.4x0.14mm, normal (0,-1,0), area 0.1mm2, adj f199,f216,f217,f253
  f201: extruded ~1.27x0.59mm, area 0.6mm2, adj f0,f202,f215,f217
  f202: extruded ~0.94x0.4mm, area 0.4mm2, adj f0,f201,f203,f217
  f203: extruded ~0.83x0.61mm, area 0.4mm2, adj f0,f202,f204,f217
  f204: extruded ~1.28x0.4mm, area 0.5mm2, adj f0,f203,f205,f217
  f205: extruded ~1.75x0.46mm, area 0.7mm2, adj f0,f204,f206,f217
  f206: extruded ~1.27x0.63mm, area 0.6mm2, adj f0,f205,f207,f217
  f207: extruded ~1.3x0.68mm, area 0.6mm2, adj f0,f206,f208,f217
  f208: plane 0.4x0.06mm, normal (1,0,0), area 0mm2, adj f0,f207,f209,f217
  f209: plane 0.6x0.4mm, normal (0.28,-0.96,0), area 0.2mm2, adj f0,f208,f210,f217
  f210: plane 1.02x0.4mm, normal (1,0,0), area 0.4mm2, adj f0,f209,f211,f217
  f211: plane 6.61x0.4mm, normal (0,1,0), area 2.6mm2, adj f0,f210,f212,f217
  f212: plane 1.25x0.4mm, normal (-1,0,0), area 0.5mm2, adj f0,f211,f213,f217
  f213: plane 1.86x0.4mm, normal (0,-1,0), area 0.7mm2, adj f0,f212,f214,f217
  f214: extruded ~0.67x0.4mm, area 0.3mm2, adj f0,f213,f215,f217
  f215: plane 0.4x0.07mm, normal (-1,0,0), area 0mm2, adj f0,f201,f214,f217
  f216: extruded ~0.94x0.4mm, area 0.4mm2, adj f194,f200,f217,f253
  f217: plane 6.7x4.29mm, normal (0,0,1), area 16.6mm2, adj f194,f195,f196,f197,f198,f199,f200,f201
  f218: plane 0.49x0.4mm, normal (-1,-0.04,0), area 0.2mm2, adj f219,f242,f243,f254
  f219: plane 0.4x0.38mm, normal (0,1,0), area 0.2mm2, adj f218,f220,f243,f254
  f220: extruded ~0.67x0.4mm, area 0.3mm2, adj f219,f221,f243,f254
  f221: extruded ~0.7x0.4mm, area 0.3mm2, adj f220,f222,f243,f254
  f222: extruded ~0.61x0.53mm, area 0.4mm2, adj f221,f223,f243,f254
  f223: extruded ~0.55x0.4mm, area 0.3mm2, adj f222,f242,f243,f254
  f224: plane 0.62x0.4mm, normal (-0.36,0.93,0), area 0.3mm2, adj f0,f225,f241,f243
  f225: plane 0.87x0.4mm, normal (-1,0,0), area 0.3mm2, adj f0,f224,f226,f243
  f226: plane 3.06x0.4mm, normal (0,-1,0), area 1.2mm2, adj f0,f225,f227,f243
  f227: extruded ~1.22x0.49mm, area 0.5mm2, adj f0,f226,f228,f243
  f228: extruded ~1.42x0.4mm, area 0.6mm2, adj f0,f227,f229,f243
  f229: extruded ~1.76x0.42mm, area 0.7mm2, adj f0,f228,f230,f243
  f230: plane 0.85x0.41mm, normal (-0.44,0.9,0), area 0.4mm2, adj f0,f229,f231,f243
  f231: extruded ~1.29x0.4mm, area 0.5mm2, adj f0,f230,f232,f243
  f232: extruded ~0.72x0.7mm, area 0.5mm2, adj f0,f231,f233,f243
  f233: plane 0.4x0.2mm, normal (0,1,0), area 0.1mm2, adj f0,f232,f234,f243
  f234: plane 0.8x0.4mm, normal (1,0.03,0), area 0.3mm2, adj f0,f233,f235,f243
  f235: extruded ~1.54x0.4mm, area 0.6mm2, adj f0,f234,f236,f243
  f236: extruded ~1.08x0.51mm, area 0.5mm2, adj f0,f235,f237,f243
  f237: extruded ~1.08x0.4mm, area 0.5mm2, adj f0,f236,f238,f243
  f238: extruded ~1.04x0.4mm, area 0.5mm2, adj f0,f237,f239,f243
  f239: extruded ~0.87x0.4mm, area 0.4mm2, adj f0,f238,f240,f243
  f240: extruded ~0.65x0.55mm, area 0.3mm2, adj f0,f239,f241,f243
  f241: plane 0.4x0.03mm, normal (-1,0,0), area 0mm2, adj f0,f224,f240,f243
  f242: extruded ~0.81x0.4mm, area 0.3mm2, adj f218,f223,f243,f254
  f243: plane 4.77x4.09mm, normal (0,0,1), area 12.9mm2, adj f218,f219,f220,f221,f222,f223,f224,f225
  f244: plane 1.27x0.4mm, normal (-1,0,0), area 0.5mm2, adj f0,f245,f251,f252
  f245: plane 4.95x0.4mm, normal (0,-1,0), area 2mm2, adj f0,f244,f246,f252
  f246: plane 1.63x0.4mm, normal (-1,0,0), area 0.7mm2, adj f0,f245,f247,f252
  f247: plane 1.06x0.4mm, normal (0,-1,0), area 0.4mm2, adj f0,f246,f248,f252
  f248: plane 4.53x0.4mm, normal (1,0,0), area 1.8mm2, adj f0,f247,f249,f252
  f249: plane 1.06x0.4mm, normal (0,1,0), area 0.4mm2, adj f0,f248,f250,f252
  f250: plane 1.63x0.4mm, normal (-1,0,0), area 0.7mm2, adj f0,f249,f251,f252
  f251: plane 4.95x0.4mm, normal (0,1,0), area 2mm2, adj f0,f244,f250,f252
  f252: plane 6x4.53mm, normal (0,0,1), area 11.1mm2, adj f244,f245,f246,f247,f248,f249,f250,f251
  f253: plane 2.74x1.76mm, normal (0,0,1), area 4.1mm2, adj f194,f195,f196,f197,f198,f199,f200,f216
  f254: plane 1.57x1.29mm, normal (0,0,1), area 1.6mm2, adj f218,f219,f220,f221,f222,f223,f242
  f255: cone r=10.5mm half-angle=80.9deg, axis (0,0,-1), area 322.1mm2, adj f9,f16
PLACE A t=(-66.27,58.99,-37.37)mm
PLACE B rot(axis=(0,0,-1),90deg) t=(0,0,34.73)mm
MATE slider A.f8 <-> B.f9  axis (0,0,1) through (0,0,0)mm
